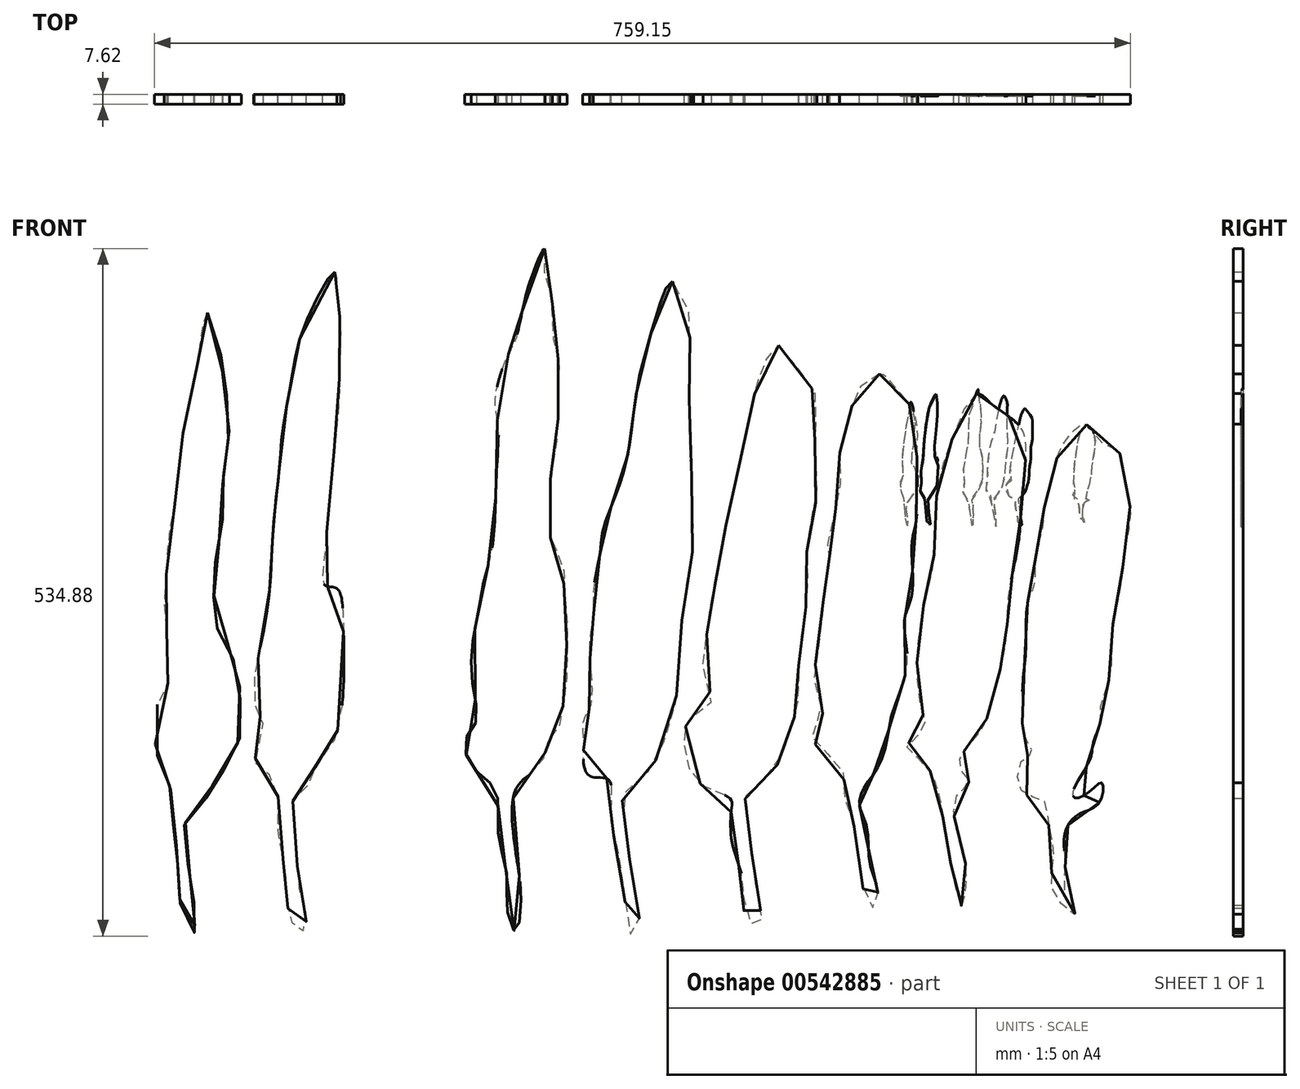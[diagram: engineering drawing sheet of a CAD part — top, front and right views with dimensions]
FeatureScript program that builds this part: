
annotation { "Feature Type Name" : "Feature", "Feature Type Description" : "" }
export const myFeature = defineFeature(function(context is Context, id is Id, definition is map)
    precondition{}
    {
        {
            var Q0;
            Q0=qCreatedBy(makeId("Front.planeOp"),FACE);
            var sketch = newSketch(context, id + "F0", { "sketchPlane" : qUnion([Q0])});
            skFitSpline(sketch, "E0", {"points": [v(-26.75, 46.41) * mm, v(-26.5, 43.12) * mm, v(-26, 39.07) * mm, v(-26, 32.23) * mm, v(-26.25, 24.64) * mm, v(-27.51, 13) * mm, v(-28.33, 2.5) * mm, v(-28.33, -2.36) * mm, v(-26.56, -2.8) * mm, v(-25.46, -7.65) * mm, v(-26.25, -24.73) * mm, v(-28.52, -28.78) * mm, v(-29.8, -30.55) * mm, v(-30.55, -33.08) * mm, v(-33.08, -35.36) * mm, v(-32.83, -41.7) * mm, v(-32.32, -49.5) * mm, v(-31.2, -54.37) * mm, v(-32.07, -56.37) * mm, v(-33.62, -54.37) * mm, v(-34.3, -49.5) * mm, v(-34.72, -45.33) * mm, v(-35.61, -40.17) * mm, v(-36.26, -32.55) * mm, v(-38.9, -30.55) * mm, v(-38.46, -26.6) * mm, v(-37.9, -23.97) * mm, v(-39.16, -20.94) * mm, v(-38.69, -13.6) * mm, v(-37.14, -5.44) * mm, v(-36.48, 4.03) * mm, v(-36.04, 9.98) * mm, v(-35.38, 15.94) * mm, v(-34.94, 21.22) * mm, v(-33.59, 29.2) * mm, v(-31.56, 37.8) * mm, v(-26.75, 46.41) * mm]});
            skFitSpline(sketch, "E1", {"points": [v(-8.5, 48.51) * mm, v(-7.65, 45.54) * mm, v(-7.65, 41.3) * mm, v(-7.65, 37.26) * mm, v(-7.86, 34.07) * mm, v(-8.29, 28.97) * mm, v(-8.71, 24.09) * mm, v(-9.35, 21.33) * mm, v(-9.14, 17.5) * mm, v(-9.77, 12.62) * mm, v(-8.71, 6.89) * mm, v(-7.65, 3.27) * mm, v(-7.44, -2.25) * mm, v(-6.8, -4.8) * mm, v(-6.8, -7.77) * mm, v(-7.22, -10.32) * mm, v(-7.86, -15) * mm, v(-8.29, -19.66) * mm, v(-9.99, -23.7) * mm, v(-11.47, -26.67) * mm, v(-12.32, -29.64) * mm, v(-15.08, -31.98) * mm, v(-16.14, -33.9) * mm, v(-16.14, -38.14) * mm, v(-15.72, -43.24) * mm, v(-15.08, -45.79) * mm, v(-14.45, -50.03) * mm, v(-14.02, -54.7) * mm, v(-14.66, -56.2) * mm, v(-15.72, -54.7) * mm, v(-16.36, -52.16) * mm, v(-16.78, -48.76) * mm, v(-17.63, -44.72) * mm, v(-18.06, -40.05) * mm, v(-18.48, -35.6) * mm, v(-19.33, -33.47) * mm, v(-22.1, -32.4) * mm, v(-23.58, -29.64) * mm, v(-23.15, -27.1) * mm, v(-22.1, -23.91) * mm, v(-22.1, -23.91) * mm, v(-21.24, -20.94) * mm, v(-22.1, -18.39) * mm, v(-22.73, -14.57) * mm, v(-22.73, -10.53) * mm, v(-22.1, -7.56) * mm, v(-21.67, -4.37) * mm, v(-21.45, 0) * mm, v(-21.03, 2.85) * mm, v(-20.18, 5.19) * mm, v(-18.48, 7.52) * mm, v(-18.48, 11.35) * mm, v(-17.84, 17.08) * mm, v(-17.2, 22.39) * mm, v(-16.57, 27.27) * mm, v(-15.72, 31.73) * mm, v(-14.87, 35.56) * mm, v(-13.6, 41.08) * mm, v(-11.68, 43.63) * mm, v(-10.4, 46.39) * mm, v(-8.5, 48.51) * mm]});
            skFitSpline(sketch, "E2", {"points": [v(-46.56, 40.04) * mm, v(-47.72, 35.4) * mm, v(-48.19, 31.7) * mm, v(-49.35, 26.59) * mm, v(-50.74, 18.7) * mm, v(-51.43, 11.74) * mm, v(-52.6, 5.25) * mm, v(-53.06, -1.94) * mm, v(-53.29, -5.88) * mm, v(-52.83, -10.3) * mm, v(-52.83, -14.47) * mm, v(-52.83, -17.95) * mm, v(-54.45, -21.2) * mm, v(-54.45, -28.59) * mm, v(-53.75, -30.24) * mm, v(-52.36, -33.95) * mm, v(-52.13, -37.66) * mm, v(-51.43, -42.53) * mm, v(-51.2, -46.47) * mm, v(-50.97, -50.65) * mm, v(-50.04, -54.82) * mm, v(-48.65, -56.45) * mm, v(-48.65, -54.13) * mm, v(-48.65, -51.58) * mm, v(-49.35, -47.63) * mm, v(-50.04, -43) * mm, v(-50.04, -39.28) * mm, v(-47.26, -36.5) * mm, v(-46.56, -34.65) * mm, v(-44.48, -31.86) * mm, v(-43.08, -29.08) * mm, v(-41.46, -25.83) * mm, v(-41.46, -21.89) * mm, v(-41.7, -16.55) * mm, v(-42.85, -13.07) * mm, v(-44.24, -9.6) * mm, v(-45.87, -8.44) * mm, v(-45.64, -4.72) * mm, v(-45.64, -1.7) * mm, v(-45.17, 2.23) * mm, v(-44.24, 7.57) * mm, v(-44.24, 11.98) * mm, v(-43.78, 17.77) * mm, v(-43.32, 20.33) * mm, v(-43.32, 25.43) * mm, v(-44.24, 30.53) * mm, v(-44.7, 35.17) * mm, v(-46.56, 40.04) * mm]});
            skFitSpline(sketch, "E3", {"points": [v(5.86, 50.01) * mm, v(5.86, 46.07) * mm, v(7.02, 42.13) * mm, v(7.02, 39.58) * mm, v(7.25, 35.87) * mm, v(8.18, 31.46) * mm, v(7.94, 27.52) * mm, v(7.94, 22.88) * mm, v(7.48, 18.47) * mm, v(6.78, 14.3) * mm, v(6.78, 9.89) * mm, v(6.78, 5.71) * mm, v(7.02, 3.63) * mm, v(8.4, 2.23) * mm, v(8.87, -2.4) * mm, v(9.33, -7.28) * mm, v(9.33, -11.22) * mm, v(9.33, -16.55) * mm, v(8.87, -20.03) * mm, v(7.94, -24.67) * mm, v(6.55, -26.3) * mm, v(5.86, -28.85) * mm, v(4.26, -31.3) * mm, v(1.32, -34.23) * mm, v(1.32, -43.58) * mm, v(1.94, -47.7) * mm, v(2.19, -52.4) * mm, v(1.32, -56.2) * mm, v(0, -52.4) * mm, v(0, -47.73) * mm, v(-1.22, -41.85) * mm, v(-1.35, -38.4) * mm, v(-1.95, -33.98) * mm, v(-5.05, -31) * mm, v(-6.5, -26.7) * mm, v(-4.8, -23.57) * mm, v(-5.22, -18.4) * mm, v(-5.45, -12.36) * mm, v(-4.55, -6.99) * mm, v(-3.66, -2.06) * mm, v(-2.54, 2.19) * mm, v(-1.87, 7.78) * mm, v(-1.62, 15.25) * mm, v(-1.37, 22.42) * mm, v(-1.8, 26.67) * mm, v(0, 33.06) * mm, v(1.32, 35.66) * mm, v(1.71, 37.09) * mm, v(2.38, 40.22) * mm, v(3.5, 44.7) * mm, v(5.86, 50.01) * mm]});
            skFitSpline(sketch, "E4", {"points": [v(-62.57, -56) * mm, v(-62.87, -50.88) * mm, v(-63.77, -44.86) * mm, v(-64.98, -39.44) * mm, v(-65.88, -34.31) * mm, v(-66.18, -27.38) * mm, v(-66.78, -19.55) * mm, v(-66.48, -14.73) * mm, v(-66.18, -8.1) * mm, v(-65.58, -2.37) * mm, v(-64.67, 3.95) * mm, v(-63.47, 10.58) * mm, v(-62.26, 15.1) * mm, v(-60.46, 18.72) * mm, v(-59.25, 15.1) * mm, v(-58.65, 10.28) * mm, v(-58.35, 2.75) * mm, v(-58.95, -3.28) * mm, v(-59.25, -10.2) * mm, v(-59.25, -15.63) * mm, v(-59.85, -19.55) * mm, v(-57.74, -24.37) * mm, v(-57.74, -28.59) * mm, v(-57.74, -28.59) * mm, v(-57.14, -34.31) * mm, v(-59.85, -38.83) * mm, v(-61.96, -42.75) * mm, v(-61.06, -51.19) * mm, v(-62.57, -56) * mm]});
            skFitSpline(sketch, "E5", {"points": [v(25.76, 44.9) * mm, v(23.67, 40.98) * mm, v(22.1, 35.74) * mm, v(20.52, 29.72) * mm, v(19.74, 24.48) * mm, v(18.95, 18.72) * mm, v(17.64, 13.49) * mm, v(16.07, 9.56) * mm, v(14.76, 5.37) * mm, v(14.5, 2.75) * mm, v(13.45, -3.27) * mm, v(13.45, -7.2) * mm, v(12.93, -10.34) * mm, v(12.93, -13.49) * mm, v(13.2, -17.94) * mm, v(12.93, -21.34) * mm, v(11.88, -23.44) * mm, v(11.88, -26.58) * mm, v(11.88, -29.46) * mm, v(12.93, -32.08) * mm, v(15.8, -32.6) * mm, v(16.07, -37.31) * mm, v(17.12, -43.34) * mm, v(18.17, -49.62) * mm, v(19.48, -56.95) * mm, v(20.52, -54.86) * mm, v(20, -50.4) * mm, v(18.95, -44.12) * mm, v(18.17, -38.1) * mm, v(18.17, -34.96) * mm, v(21.3, -32.08) * mm, v(24.19, -27.36) * mm, v(26.28, -20.3) * mm, v(27.07, -10.87) * mm, v(27.6, -4.58) * mm, v(28.9, 3.27) * mm, v(28.9, 10.87) * mm, v(28.38, 22.13) * mm, v(28.38, 28.67) * mm, v(28.38, 34.7) * mm, v(28.38, 39.93) * mm, v(25.76, 44.9) * mm]});
            skFitSpline(sketch, "E6", {"points": [v(42.26, 34.96) * mm, v(45.14, 31.55) * mm, v(48.02, 27.1) * mm, v(48.02, 23.17) * mm, v(48.02, 16.1) * mm, v(48.02, 10.34) * mm, v(46.7, 5.37) * mm, v(46.7, 2.23) * mm, v(46.7, -3.54) * mm, v(46.19, -7.72) * mm, v(45.4, -14.27) * mm, v(45.4, -18.98) * mm, v(44.61, -23.17) * mm, v(43.57, -26.32) * mm, v(41.2, -31.55) * mm, v(37.8, -34.17) * mm, v(37.02, -36.27) * mm, v(37.8, -41.24) * mm, v(38.33, -46.74) * mm, v(39.38, -52.5) * mm, v(39.38, -55.9) * mm, v(37.02, -53.55) * mm, v(37.02, -50.4) * mm, v(36.23, -46.48) * mm, v(34.93, -41.77) * mm, v(34.93, -37.31) * mm, v(34.66, -35.48) * mm, v(29.95, -33.12) * mm, v(27.6, -26.84) * mm, v(28.64, -22.91) * mm, v(31.78, -20.56) * mm, v(30.74, -16.63) * mm, v(31, -10.87) * mm, v(31.78, -5.1) * mm, v(32.3, -2.49) * mm, v(33.35, 3.27) * mm, v(34.66, 9.82) * mm, v(36.23, 16.89) * mm, v(38.07, 25.53) * mm, v(39.64, 31.03) * mm, v(42.26, 34.96) * mm]});
            skFitSpline(sketch, "E7", {"points": [v(90.18, 22.65) * mm, v(92.27, 20.03) * mm, v(95.15, 18.46) * mm, v(95.94, 14.8) * mm, v(96.99, 9.56) * mm, v(96.2, 3.54) * mm, v(95.41, -2.75) * mm, v(94.37, -7.72) * mm, v(94.1, -11.4) * mm, v(93.58, -17.41) * mm, v(92.27, -21.34) * mm, v(92.27, -23.7) * mm, v(91.22, -26.84) * mm, v(90.7, -29.46) * mm, v(88.08, -34.43) * mm, v(88.34, -35.48) * mm, v(90.7, -34.43) * mm, v(92.53, -33.12) * mm, v(92.27, -36) * mm, v(89.92, -37.58) * mm, v(88.08, -38.62) * mm, v(86.77, -40.98) * mm, v(86.77, -44.12) * mm, v(86.77, -47) * mm, v(87.03, -51.45) * mm, v(88.34, -53.55) * mm, v(85.17, -50.6) * mm, v(84.94, -45.96) * mm, v(84.94, -42.45) * mm, v(84.15, -38.62) * mm, v(83.63, -36) * mm, v(80.75, -34.96) * mm, v(79.44, -32.08) * mm, v(80.75, -28.94) * mm, v(81.8, -28.67) * mm, v(80.49, -25.8) * mm, v(80.23, -23.2) * mm, v(80.23, -17.94) * mm, v(80.75, -11.91) * mm, v(81.01, -5.1) * mm, v(82.06, -2.23) * mm, v(82.32, 2.49) * mm, v(83.37, 6.68) * mm, v(83.63, 9.82) * mm, v(84.68, 13.75) * mm, v(85.73, 17.94) * mm, v(88.08, 21.6) * mm, v(90.18, 22.65) * mm]});
            skFitSpline(sketch, "E8", {"points": [v(57.98, 30.54) * mm, v(54.5, 27.83) * mm, v(53.34, 23.96) * mm, v(51.8, 18.55) * mm, v(51.8, 12.37) * mm, v(49.86, 4.25) * mm, v(50.25, 1.93) * mm, v(49.47, -2.32) * mm, v(48.7, -10.44) * mm, v(47.93, -18.55) * mm, v(49.09, -22.42) * mm, v(47.93, -23.58) * mm, v(47.93, -27.06) * mm, v(51.8, -30.15) * mm, v(52.57, -35.56) * mm, v(54.11, -40.2) * mm, v(55.27, -49.09) * mm, v(57.2, -52.57) * mm, v(57.6, -49.47) * mm, v(56.43, -45.6) * mm, v(56.04, -40.2) * mm, v(54.88, -36.72) * mm, v(55.27, -34.4) * mm, v(56.82, -32.08) * mm, v(58.75, -28.22) * mm, v(59.9, -22.42) * mm, v(62.23, -14.69) * mm, v(61.84, -7.72) * mm, v(63, -3.87) * mm, v(63, 3.87) * mm, v(63.77, 8.5) * mm, v(63.77, 17.78) * mm, v(63.39, 24.35) * mm, v(59.9, 28.99) * mm, v(57.98, 30.54) * mm]});
            skFitSpline(sketch, "E9", {"points": [v(73.05, 27.44) * mm, v(69.57, 21.26) * mm, v(66.87, 11.98) * mm, v(66.48, 2.32) * mm, v(64.93, -5.02) * mm, v(63.77, -13.91) * mm, v(64.55, -22.03) * mm, v(64.93, -24.74) * mm, v(62.23, -27.44) * mm, v(64.93, -30.15) * mm, v(67.25, -35.17) * mm, v(68.41, -42.13) * mm, v(69.57, -48.32) * mm, v(70.73, -52.18) * mm, v(71.5, -47.54) * mm, v(70.35, -41.74) * mm, v(69.96, -35.17) * mm, v(71.9, -32.85) * mm, v(70.35, -30.54) * mm, v(72.66, -26.28) * mm, v(74.6, -23.2) * mm, v(76.53, -16.23) * mm, v(77.69, -10.44) * mm, v(78.08, -3.87) * mm, v(79.62, 4.64) * mm, v(80.23, 13.14) * mm, v(80.23, 21.65) * mm, v(75.76, 25.51) * mm, v(73.05, 27.44) * mm]});
            skSolve(sketch);
        }
        {
            var Q0;
            Q0=qSketchRegion(id+"F0",true);
            extrude(context, id + "F1", {"entities" : qUnion([Q0]), "depth" : 1.52 * mm, "offsetDistance" : 25.4 * mm});
        }
        {
            var Q0;
            Q0=makeQuery(id+"F1.opExtrude","SWEPT_BODY",BODY,{"disambiguationData":[OSD([sQuery(id+"F0.wireOp",EDGE,"E4")])]});
            var Q1;
            Q1=makeQuery(id+"F1.opExtrude","SWEPT_BODY",BODY,{"disambiguationData":[OSD([sQuery(id+"F0.wireOp",EDGE,"E2")])]});
            var Q2;
            Q2=makeQuery(id+"F1.opExtrude","SWEPT_BODY",BODY,{"disambiguationData":[OSD([sQuery(id+"F0.wireOp",EDGE,"E1")])]});
            var Q3;
            Q3=makeQuery(id+"F1.opExtrude","SWEPT_BODY",BODY,{"disambiguationData":[OSD([sQuery(id+"F0.wireOp",EDGE,"E0")])]});
            var Q4;
            Q4=makeQuery(id+"F1.opExtrude","SWEPT_BODY",BODY,{"disambiguationData":[OSD([sQuery(id+"F0.wireOp",EDGE,"E3")])]});
            var Q5;
            Q5=makeQuery(id+"F1.opExtrude","SWEPT_BODY",BODY,{"disambiguationData":[OSD([sQuery(id+"F0.wireOp",EDGE,"E5")])]});
            var Q6;
            Q6=makeQuery(id+"F1.opExtrude","SWEPT_BODY",BODY,{"disambiguationData":[OSD([sQuery(id+"F0.wireOp",EDGE,"E6")])]});
            var Q7;
            Q7=makeQuery(id+"F1.opExtrude","SWEPT_BODY",BODY,{"disambiguationData":[OSD([sQuery(id+"F0.wireOp",EDGE,"E8")])]});
            var Q8;
            Q8=makeQuery(id+"F1.opExtrude","SWEPT_BODY",BODY,{"disambiguationData":[OSD([sQuery(id+"F0.wireOp",EDGE,"E9")])]});
            var Q9;
            Q9=makeQuery(id+"F1.opExtrude","SWEPT_BODY",BODY,{"disambiguationData":[OSD([sQuery(id+"F0.wireOp",EDGE,"E7")])]});
            var Q10;
            Q10=sQuery(id+"F0.wireOp",VERTEX,"E7.0.internal");
            transform(context, id + "F2", {"entities" : qUnion([Q0, Q1, Q2, Q3, Q4, Q5, Q6, Q7, Q8, Q9]), "transformType" : TransformType.SCALE_UNIFORMLY, "scale" : 5, "scalePoint" : qUnion([Q10]), "makeCopy" : false});
        }
        {
            var Q0;
            Q0=makeQuery(id+"F1.opExtrude","CAP_FACE",FACE,{"disambiguationData":[OSD([sQuery(id+"F0.wireOp",EDGE,"E4")])],"isStart":false});
            var sketch = newSketch(context, id + "F3", { "sketchPlane" : qUnion([Q0])});
            skPoint(sketch, "E10", {"position": v(87.01, 21.31) * mm});
            skPoint(sketch, "E11", {"position": v(82.1, -244.62) * mm});
            skPoint(sketch, "E12", {"position": v(64.9, -40.1) * mm});
            skPoint(sketch, "E13", {"position": v(112.8, -26.6) * mm});
            skSolve(sketch);
        }
        {
            var Q0;
            Q0=makeQuery(id+"F1.opExtrude","CAP_FACE",FACE,{"disambiguationData":[OSD([sQuery(id+"F0.wireOp",EDGE,"E5")])],"isStart":false});
            var sketch = newSketch(context, id + "F4", { "sketchPlane" : qUnion([Q0])});
            skFitSpline(sketch, "E14.0.0", {"points": [v(-231.9, 133.94) * mm, v(-236.24, 134.07) * mm, v(-243.4, 111.19) * mm, v(-250.08, 88.9) * mm, v(-258.89, 57.85) * mm, v(-262.03, 32) * mm, v(-265.31, 3.14) * mm, v(-271.76, -23.43) * mm, v(-280.43, -41.92) * mm, v(-287.99, -64.08) * mm, v(-287.13, -76.64) * mm, v(-295.36, -107.28) * mm, v(-292.07, -126.07) * mm, v(-296.99, -142.46) * mm, v(-296.09, -158.13) * mm, v(-294.61, -179.91) * mm, v(-294.2, -197.7) * mm, v(-303.4, -207.13) * mm, v(-300.57, -224.02) * mm, v(-302.03, -236.97) * mm, v(-299.05, -255.03) * mm, v(-275.65, -248.5) * mm, v(-283.17, -279.51) * mm, v(-274.23, -308.31) * mm, v(-269.75, -334.19) * mm, v(-265.86, -386.05) * mm, v(-255.48, -362.43) * mm, v(-261.36, -342.38) * mm, v(-266.21, -311.48) * mm, v(-269.2, -282.05) * mm, v(-273.58, -263.7) * mm, v(-251.4, -252.03) * mm, v(-238.7, -226.89) * mm, v(-227.28, -192.54) * mm, v(-225.42, -144.54) * mm, v(-223.86, -114.1) * mm, v(-214.3, -73.1) * mm, v(-216.06, -37.02) * mm, v(-219.5, 20.22) * mm, v(-218.38, 51.48) * mm, v(-219.89, 83.74) * mm, v(-215.14, 106.23) * mm, v(-227.04, 133.8) * mm, v(-231.9, 133.94) * mm]});
            skFitSpline(sketch, "E15.0.0", {"points": [v(-331.43, 159.47) * mm, v(-333, 159.71) * mm, v(-345.34, 129.75) * mm, v(-348.27, 112.15) * mm, v(-352.18, 94.93) * mm, v(-353.64, 87.23) * mm, v(-361.89, 74.67) * mm, v(-372.55, 41.93) * mm, v(-365.66, 21.77) * mm, v(-369.53, -15.04) * mm, v(-369.4, -50.98) * mm, v(-372.44, -79.61) * mm, v(-379.72, -100.73) * mm, v(-383.13, -125.9) * mm, v(-389.17, -152.4) * mm, v(-388.22, -181.86) * mm, v(-380.15, -209.35) * mm, v(-397.9, -222.86) * mm, v(-387.86, -248.28) * mm, v(-366.8, -257.68) * mm, v(-367.37, -283.54) * mm, v(-368.26, -299.5) * mm, v(-358.1, -330.31) * mm, v(-363.3, -349.42) * mm, v(-353.27, -382.17) * mm, v(-348.53, -349.87) * mm, v(-350.9, -328.68) * mm, v(-354.12, -309.46) * mm, v(-360.9, -258.69) * mm, v(-338.5, -248.6) * mm, v(-330.34, -235.62) * mm, v(-329.7, -220.84) * mm, v(-318.36, -215.36) * mm, v(-316.78, -189.56) * mm, v(-313.1, -174.04) * mm, v(-314.5, -146.23) * mm, v(-313.14, -126.98) * mm, v(-317.54, -103.63) * mm, v(-315.21, -78.24) * mm, v(-327.6, -73.5) * mm, v(-326.51, -61.24) * mm, v(-326.61, -40.8) * mm, v(-327.82, -19.1) * mm, v(-322.9, 1.77) * mm, v(-320.24, 23.67) * mm, v(-321.99, 47.03) * mm, v(-317.91, 66.69) * mm, v(-325.5, 88.33) * mm, v(-326.15, 107.06) * mm, v(-323.84, 120.85) * mm, v(-334.34, 136.82) * mm, v(-330.14, 159.27) * mm, v(-331.43, 159.47) * mm]});
            skSolve(sketch);
        }
        {
            var Q0;
            Q0=makeQuery(id+"F0.imprint","IMPRINT",FACE,{"disambiguationData":[TD([[makeQuery(id+"F0.imprint","IMPRINT",EDGE,{"derivedFrom":sQuery(id+"F0.wireOp",EDGE,"E4")}),-1.0]])]});
            var Q1;
            Q1=makeQuery(id+"F0.imprint","IMPRINT",FACE,{"disambiguationData":[TD([[makeQuery(id+"F0.imprint","IMPRINT",EDGE,{"derivedFrom":sQuery(id+"F0.wireOp",EDGE,"E2")}),1.0]])]});
            var Q2;
            Q2=makeQuery(id+"F0.imprint","IMPRINT",FACE,{"disambiguationData":[TD([[makeQuery(id+"F0.imprint","IMPRINT",EDGE,{"derivedFrom":sQuery(id+"F0.wireOp",EDGE,"E0")}),-1.0]])]});
            var Q3;
            Q3=makeQuery(id+"F0.imprint","IMPRINT",FACE,{"disambiguationData":[TD([[makeQuery(id+"F0.imprint","IMPRINT",EDGE,{"derivedFrom":sQuery(id+"F0.wireOp",EDGE,"E1")}),-1.0]])]});
            var Q4;
            Q4=makeQuery(id+"F0.imprint","IMPRINT",FACE,{"disambiguationData":[TD([[makeQuery(id+"F0.imprint","IMPRINT",EDGE,{"derivedFrom":sQuery(id+"F0.wireOp",EDGE,"E3")}),-1.0]])]});
            var Q5;
            Q5=makeQuery(id+"F0.imprint","IMPRINT",FACE,{"disambiguationData":[TD([[makeQuery(id+"F0.imprint","IMPRINT",EDGE,{"derivedFrom":sQuery(id+"F0.wireOp",EDGE,"E5")}),1.0]])]});
            var Q6;
            Q6=makeQuery(id+"F0.imprint","IMPRINT",FACE,{"disambiguationData":[TD([[makeQuery(id+"F0.imprint","IMPRINT",EDGE,{"derivedFrom":sQuery(id+"F0.wireOp",EDGE,"E6")}),-1.0]])]});
            var Q7;
            Q7=makeQuery(id+"F0.imprint","IMPRINT",FACE,{"disambiguationData":[TD([[makeQuery(id+"F0.imprint","IMPRINT",EDGE,{"derivedFrom":sQuery(id+"F0.wireOp",EDGE,"E7")}),-1.0]])]});
            extrude(context, id + "F5", {"entities" : qUnion([Q0, Q1, Q2, Q3, Q4, Q5, Q6, Q7]), "depth" : 1.52 * mm, "offsetDistance" : 25.4 * mm});
        }
    });
